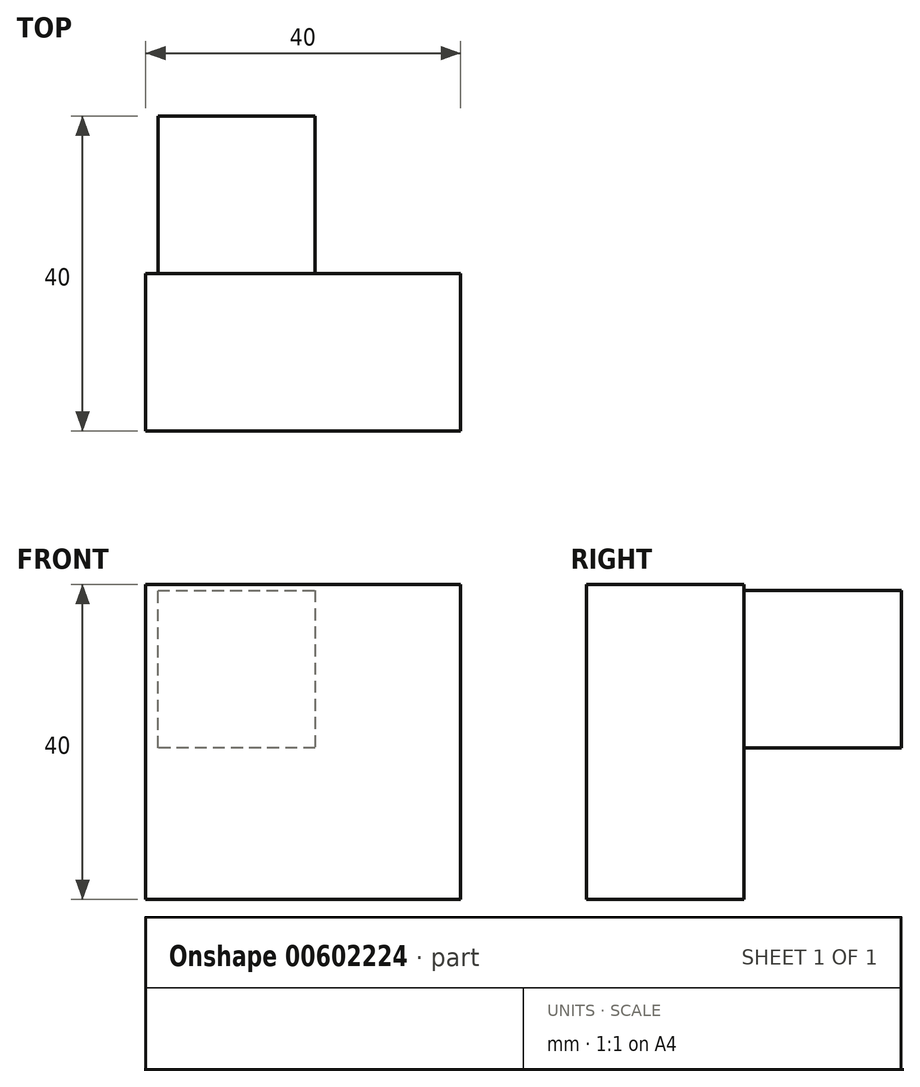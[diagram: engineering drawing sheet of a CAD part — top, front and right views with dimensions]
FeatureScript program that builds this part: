
annotation { "Feature Type Name" : "Feature", "Feature Type Description" : "" }
export const myFeature = defineFeature(function(context is Context, id is Id, definition is map)
    precondition{}
    {
        {
            var Q0;
            Q0=qCreatedBy(makeId("Front.planeOp"),FACE);
            var sketch = newSketch(context, id + "F0", { "sketchPlane" : qUnion([Q0])});
            skLineSegment(sketch, "E0", {"start": v(-46.97, 28.93) * mm, "end": v(-6.97, 28.93) * mm});
            skLineSegment(sketch, "E1", {"start": v(-6.97, 28.93) * mm, "end": v(-6.97, -11.07) * mm});
            skLineSegment(sketch, "E2", {"start": v(-6.97, -11.07) * mm, "end": v(-46.97, -11.07) * mm});
            skLineSegment(sketch, "E3", {"start": v(-46.97, -11.07) * mm, "end": v(-46.97, 28.93) * mm});
            skSolve(sketch);
        }
        {
            var Q0;
            Q0=makeQuery(id+"F0.imprint","IMPRINT",FACE,{"disambiguationData":[TD([[makeQuery(id+"F0.imprint","IMPRINT",EDGE,{"derivedFrom":sQuery(id+"F0.wireOp",EDGE,"E0")}),-1.0]])]});
            extrude(context, id + "F1", {"entities" : qUnion([Q0]), "depth" : 20 * mm, "offsetDistance" : 25 * mm});
        }
        {
            var Q0;
            Q0=qCreatedBy(makeId("Front.planeOp"),FACE);
            var sketch = newSketch(context, id + "F2", { "sketchPlane" : qUnion([Q0])});
            skLineSegment(sketch, "E4", {"start": v(-45.43, 28.19) * mm, "end": v(-25.43, 28.19) * mm});
            skLineSegment(sketch, "E5", {"start": v(-25.43, 28.19) * mm, "end": v(-25.43, 8.19) * mm});
            skLineSegment(sketch, "E6", {"start": v(-25.43, 8.19) * mm, "end": v(-45.43, 8.19) * mm});
            skLineSegment(sketch, "E7", {"start": v(-45.43, 8.19) * mm, "end": v(-45.43, 28.19) * mm});
            skSolve(sketch);
        }
        {
            var Q0;
            Q0=makeQuery(id+"F2.imprint","IMPRINT",FACE,{"disambiguationData":[TD([[makeQuery(id+"F2.imprint","IMPRINT",EDGE,{"derivedFrom":sQuery(id+"F2.wireOp",EDGE,"E4")}),-1.0]])]});
            extrude(context, id + "F3", {"entities" : qUnion([Q0]), "operationType" : NewBodyOperationType.ADD, "oppositeDirection" : true, "depth" : 20 * mm, "offsetDistance" : 25 * mm});
        }
    });
